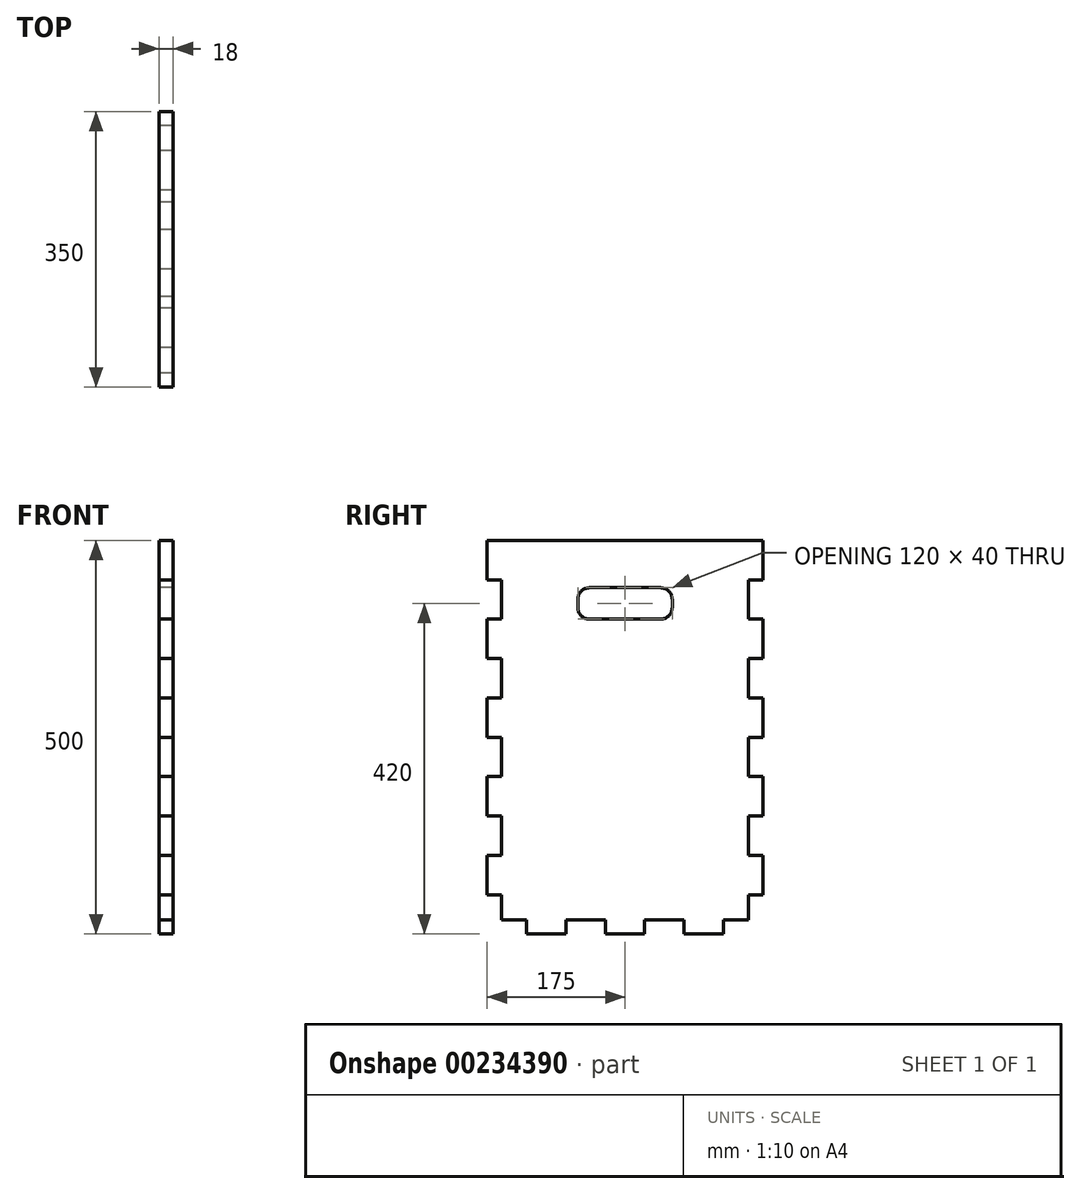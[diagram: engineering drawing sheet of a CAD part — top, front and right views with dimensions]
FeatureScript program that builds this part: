
annotation { "Feature Type Name" : "Feature", "Feature Type Description" : "" }
export const myFeature = defineFeature(function(context is Context, id is Id, definition is map)
    precondition{}
    {
        {
            var Q0;
            Q0=qCreatedBy(makeId("Right.planeOp"),FACE);
            var sketch = newSketch(context, id + "F0", { "sketchPlane" : qUnion([Q0])});
            skLineSegment(sketch, "E0.bottom", {"start": v(157, 250) * mm, "end": v(-157, 250) * mm});
            skLineSegment(sketch, "E0.left", {"start": v(175, 150) * mm, "end": v(175, 100) * mm});
            skPoint(sketch, "E0.middle", {"position": v(0, 0) * mm});
            skLineSegment(sketch, "E1.top", {"start": v(175, 200) * mm, "end": v(157, 200) * mm});
            skLineSegment(sketch, "E2.top", {"start": v(175, 150) * mm, "end": v(157, 150) * mm});
            skLineSegment(sketch, "E2.right", {"start": v(157, 200) * mm, "end": v(157, 150) * mm});
            skLineSegment(sketch, "E3.top", {"start": v(175, 100) * mm, "end": v(157, 100) * mm});
            skLineSegment(sketch, "E4.top", {"start": v(175, 50) * mm, "end": v(157, 50) * mm});
            skLineSegment(sketch, "E4.right", {"start": v(157, 100) * mm, "end": v(157, 50) * mm});
            skLineSegment(sketch, "E5.top", {"start": v(175, 0) * mm, "end": v(157, 0) * mm});
            skLineSegment(sketch, "E5.left", {"start": v(175, 50) * mm, "end": v(175, 0) * mm});
            skLineSegment(sketch, "E6.top", {"start": v(175, -50) * mm, "end": v(157, -50) * mm});
            skLineSegment(sketch, "E6.right", {"start": v(157, 0) * mm, "end": v(157, -50) * mm});
            skLineSegment(sketch, "E7.top", {"start": v(175, -100) * mm, "end": v(157, -100) * mm});
            skLineSegment(sketch, "E7.left", {"start": v(175, -50) * mm, "end": v(175, -100) * mm});
            skLineSegment(sketch, "E8.top", {"start": v(175, -150) * mm, "end": v(157, -150) * mm});
            skLineSegment(sketch, "E8.right", {"start": v(157, -100) * mm, "end": v(157, -150) * mm});
            skLineSegment(sketch, "E9.top", {"start": v(175, -200) * mm, "end": v(157, -200) * mm});
            skLineSegment(sketch, "E9.left", {"start": v(175, -150) * mm, "end": v(175, -200) * mm});
            skLineSegment(sketch, "E10.right", {"start": v(157, -200) * mm, "end": v(157, -232) * mm});
            skLineSegment(sketch, "E11.top", {"start": v(-175, 200) * mm, "end": v(-157, 200) * mm});
            skLineSegment(sketch, "E12.bottom", {"start": v(-157, 200) * mm, "end": v(-175, 200) * mm});
            skLineSegment(sketch, "E12.top", {"start": v(-157, 150) * mm, "end": v(-175, 150) * mm});
            skLineSegment(sketch, "E13.top", {"start": v(-157, 100) * mm, "end": v(-175, 100) * mm});
            skLineSegment(sketch, "E14.top", {"start": v(-157, 50) * mm, "end": v(-175, 50) * mm});
            skLineSegment(sketch, "E15.top", {"start": v(-157, 0) * mm, "end": v(-175, 0) * mm});
            skLineSegment(sketch, "E16.top", {"start": v(-157, -50) * mm, "end": v(-175, -50) * mm});
            skLineSegment(sketch, "E17.top", {"start": v(-157, -100) * mm, "end": v(-175, -100) * mm});
            skLineSegment(sketch, "E18.top", {"start": v(-157, -150) * mm, "end": v(-175, -150) * mm});
            skLineSegment(sketch, "E19.top", {"start": v(-157, -200) * mm, "end": v(-175, -200) * mm});
            skPoint(sketch, "E11.left.start.orphan", {"position": v(-175, 250) * mm});
            skPoint(sketch, "E20.orphan", {"position": v(175, 250) * mm});
            skLineSegment(sketch, "E21.bottom", {"start": v(175, 250) * mm, "end": v(157, 250) * mm});
            skLineSegment(sketch, "E21.left", {"start": v(175, 250) * mm, "end": v(175, 200) * mm});
            skPoint(sketch, "E22.orphan", {"position": v(175, -250) * mm});
            skLineSegment(sketch, "E23.right", {"start": v(-125, -250) * mm, "end": v(-125, -232) * mm});
            skLineSegment(sketch, "E24.left", {"start": v(-125, -232) * mm, "end": v(-125, -250) * mm});
            skLineSegment(sketch, "E24.right", {"start": v(-75, -232) * mm, "end": v(-75, -250) * mm});
            skLineSegment(sketch, "E25.right", {"start": v(-25, -232) * mm, "end": v(-25, -250) * mm});
            skLineSegment(sketch, "E26.right", {"start": v(25, -232) * mm, "end": v(25, -250) * mm});
            skLineSegment(sketch, "E27.right", {"start": v(75, -232) * mm, "end": v(75, -250) * mm});
            skLineSegment(sketch, "E28.right", {"start": v(125, -232) * mm, "end": v(125, -250) * mm});
            skPoint(sketch, "E29.orphan", {"position": v(-175, -250) * mm});
            skLineSegment(sketch, "E30.bottom", {"start": v(-157, 250) * mm, "end": v(-175, 250) * mm});
            skLineSegment(sketch, "E30.left", {"start": v(-157, 200) * mm, "end": v(-157, 150) * mm});
            skLineSegment(sketch, "E30.right", {"start": v(-175, 250) * mm, "end": v(-175, 200) * mm});
            skLineSegment(sketch, "E31.trimOffspring", {"start": v(-175, 150) * mm, "end": v(-175, 100) * mm});
            skLineSegment(sketch, "E32.trimOffspring", {"start": v(-157, 100) * mm, "end": v(-157, 50) * mm});
            skLineSegment(sketch, "E33.trimOffspring", {"start": v(-175, 50) * mm, "end": v(-175, 0) * mm});
            skLineSegment(sketch, "E34.trimOffspring", {"start": v(-157, 0) * mm, "end": v(-157, -50) * mm});
            skLineSegment(sketch, "E35.trimOffspring", {"start": v(-175, -50) * mm, "end": v(-175, -100) * mm});
            skLineSegment(sketch, "E36.trimOffspring", {"start": v(-157, -100) * mm, "end": v(-157, -150) * mm});
            skLineSegment(sketch, "E37.trimOffspring", {"start": v(-175, -150) * mm, "end": v(-175, -200) * mm});
            skLineSegment(sketch, "E38.trimOffspring", {"start": v(-157, -200) * mm, "end": v(-157, -232) * mm});
            skLineSegment(sketch, "E39.bottom", {"start": v(-157, -232) * mm, "end": v(-125, -232) * mm});
            skLineSegment(sketch, "E39.top", {"start": v(-125, -250) * mm, "end": v(-75, -250) * mm});
            skLineSegment(sketch, "E40.trimOffspring", {"start": v(-75, -232) * mm, "end": v(-25, -232) * mm});
            skLineSegment(sketch, "E41.trimOffspring", {"start": v(-25, -250) * mm, "end": v(25, -250) * mm});
            skLineSegment(sketch, "E42.trimOffspring", {"start": v(25, -232) * mm, "end": v(75, -232) * mm});
            skLineSegment(sketch, "E43", {"start": v(125, -250) * mm, "end": v(75, -250) * mm});
            skLineSegment(sketch, "E44.trimOffspring", {"start": v(125, -232) * mm, "end": v(157, -232) * mm});
            skPoint(sketch, "E45.orphan", {"position": v(157, -250) * mm});
            skSolve(sketch);
        }
        {
            var Q0;
            Q0 = qSketchRegion(id + "F0", true);
            extrude(context, id + "F1", {"entities" : qUnion([Q0]), "depth" : 18 * mm});
        }
        {
            var Q0;
            Q0=makeQuery(id+"F1.opExtrude","CAP_FACE",FACE,{"disambiguationData":[OSD([sQuery(id+"F0.wireOp",EDGE,"E0.bottom"),sQuery(id+"F0.wireOp",EDGE,"E2.right"),sQuery(id+"F0.wireOp",EDGE,"E2.top"),sQuery(id+"F0.wireOp",EDGE,"E0.left"),sQuery(id+"F0.wireOp",EDGE,"E3.top"),sQuery(id+"F0.wireOp",EDGE,"E4.right"),sQuery(id+"F0.wireOp",EDGE,"E4.top"),sQuery(id+"F0.wireOp",EDGE,"E5.top"),sQuery(id+"F0.wireOp",EDGE,"E6.right"),sQuery(id+"F0.wireOp",EDGE,"E6.top"),sQuery(id+"F0.wireOp",EDGE,"E7.top"),sQuery(id+"F0.wireOp",EDGE,"E8.right"),sQuery(id+"F0.wireOp",EDGE,"E8.top"),sQuery(id+"F0.wireOp",EDGE,"E9.top"),sQuery(id+"F0.wireOp",EDGE,"E10.right"),sQuery(id+"F0.wireOp",EDGE,"E12.bottom"),sQuery(id+"F0.wireOp",EDGE,"E12.top"),sQuery(id+"F0.wireOp",EDGE,"E13.top"),sQuery(id+"F0.wireOp",EDGE,"E14.top"),sQuery(id+"F0.wireOp",EDGE,"E15.top"),sQuery(id+"F0.wireOp",EDGE,"E16.top"),sQuery(id+"F0.wireOp",EDGE,"E17.top"),sQuery(id+"F0.wireOp",EDGE,"E18.top"),sQuery(id+"F0.wireOp",EDGE,"E19.top"),sQuery(id+"F0.wireOp",EDGE,"E21.bottom"),sQuery(id+"F0.wireOp",EDGE,"E1.top"),sQuery(id+"F0.wireOp",EDGE,"E21.left"),sQuery(id+"F0.wireOp",EDGE,"E5.left"),sQuery(id+"F0.wireOp",EDGE,"E7.left"),sQuery(id+"F0.wireOp",EDGE,"E9.left"),sQuery(id+"F0.wireOp",EDGE,"E24.left"),sQuery(id+"F0.wireOp",EDGE,"E24.right"),sQuery(id+"F0.wireOp",EDGE,"E25.right"),sQuery(id+"F0.wireOp",EDGE,"E26.right"),sQuery(id+"F0.wireOp",EDGE,"E27.right"),sQuery(id+"F0.wireOp",EDGE,"E28.right"),sQuery(id+"F0.wireOp",EDGE,"E30.bottom"),sQuery(id+"F0.wireOp",EDGE,"E30.left"),sQuery(id+"F0.wireOp",EDGE,"E30.right"),sQuery(id+"F0.wireOp",EDGE,"E31.trimOffspring"),sQuery(id+"F0.wireOp",EDGE,"E32.trimOffspring"),sQuery(id+"F0.wireOp",EDGE,"E33.trimOffspring"),sQuery(id+"F0.wireOp",EDGE,"E34.trimOffspring"),sQuery(id+"F0.wireOp",EDGE,"E35.trimOffspring"),sQuery(id+"F0.wireOp",EDGE,"E36.trimOffspring"),sQuery(id+"F0.wireOp",EDGE,"E37.trimOffspring"),sQuery(id+"F0.wireOp",EDGE,"E38.trimOffspring"),sQuery(id+"F0.wireOp",EDGE,"E39.bottom"),sQuery(id+"F0.wireOp",EDGE,"E39.top"),sQuery(id+"F0.wireOp",EDGE,"E40.trimOffspring"),sQuery(id+"F0.wireOp",EDGE,"E41.trimOffspring"),sQuery(id+"F0.wireOp",EDGE,"E42.trimOffspring"),sQuery(id+"F0.wireOp",EDGE,"E43"),sQuery(id+"F0.wireOp",EDGE,"E44.trimOffspring")])],"isStart":true});
            var sketch = newSketch(context, id + "F2", { "sketchPlane" : qUnion([Q0])});
            skLineSegment(sketch, "E46.bottom", {"start": v(-45, 190) * mm, "end": v(45, 190) * mm});
            skLineSegment(sketch, "E46.top", {"start": v(-45, 150) * mm, "end": v(45, 150) * mm});
            skLineSegment(sketch, "E46.left", {"start": v(-60, 175) * mm, "end": v(-60, 165) * mm});
            skLineSegment(sketch, "E46.right", {"start": v(60, 175) * mm, "end": v(60, 165) * mm});
            skPoint(sketch, "E46.middle", {"position": v(0, 170) * mm});
            skPoint(sketch, "E47.visualSharp", {"position": v(-60, 190) * mm});
            skArc(sketch, "E47.filletArc", {"start": v(-45, 190) * mm, "mid": v(-55.6, 185.6) * mm, "end": v(-60, 175) * mm});
            skPoint(sketch, "E48.visualSharp", {"position": v(60, 190) * mm});
            skArc(sketch, "E48.filletArc", {"start": v(60, 175) * mm, "mid": v(55.6, 185.6) * mm, "end": v(45, 190) * mm});
            skPoint(sketch, "E49.visualSharp", {"position": v(60, 150) * mm});
            skArc(sketch, "E49.filletArc", {"start": v(45, 150) * mm, "mid": v(55.6, 154.4) * mm, "end": v(60, 165) * mm});
            skPoint(sketch, "E50.visualSharp", {"position": v(-60, 150) * mm});
            skArc(sketch, "E50.filletArc", {"start": v(-60, 165) * mm, "mid": v(-55.6, 154.4) * mm, "end": v(-45, 150) * mm});
            skSolve(sketch);
        }
        {
            var Q0;
            Q0 = qSketchRegion(id + "F2", true);
            extrude(context, id + "F3", {"entities" : qUnion([Q0]), "operationType" : NewBodyOperationType.REMOVE, "oppositeDirection" : true, "depth" : 25 * mm});
        }
    });
